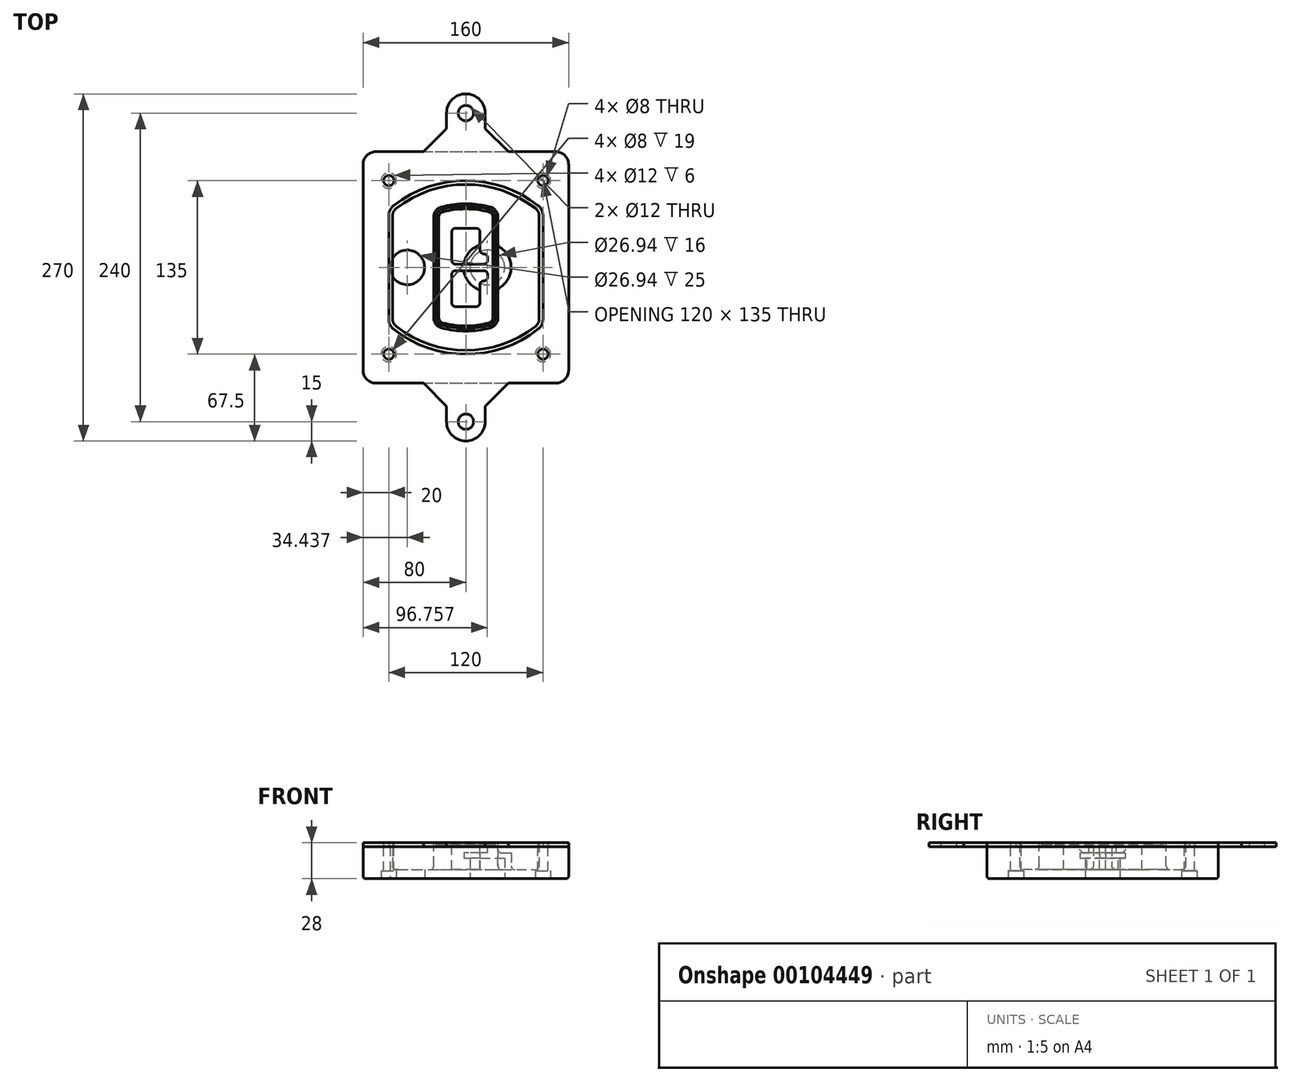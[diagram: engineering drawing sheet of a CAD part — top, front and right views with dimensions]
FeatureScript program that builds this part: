
annotation { "Feature Type Name" : "Feature", "Feature Type Description" : "" }
export const myFeature = defineFeature(function(context is Context, id is Id, definition is map)
    precondition{}
    {
        {
            var Q0;
            Q0=qCreatedBy(makeId("Top.planeOp"),FACE);
            var sketch = newSketch(context, id + "F0", { "sketchPlane" : qUnion([Q0])});
            skPoint(sketch, "E0.rect.middle", {"position": v(0, 0) * mm});
            skLineSegment(sketch, "E1.bottom", {"start": v(-70, -90) * mm, "end": v(70, -90) * mm});
            skLineSegment(sketch, "E1.top", {"start": v(-70, 90) * mm, "end": v(70, 90) * mm});
            skLineSegment(sketch, "E1.left", {"start": v(-80, -80) * mm, "end": v(-80, 80) * mm});
            skLineSegment(sketch, "E1.right", {"start": v(80, -80) * mm, "end": v(80, 80) * mm});
            skLineSegment(sketch, "E2", {"start": v(-80, 90) * mm, "end": v(80, -90) * mm, "construction": true});
            skLineSegment(sketch, "E3", {"start": v(80, 90) * mm, "end": v(-80, -90) * mm, "construction": true});
            skCircle(sketch, "E4", {"center": v(-60, 67.5) * mm, "radius": 4 * mm});
            skCircle(sketch, "E5", {"center": v(60, 67.5) * mm, "radius": 4 * mm});
            skCircle(sketch, "E6", {"center": v(60, -67.5) * mm, "radius": 4 * mm});
            skCircle(sketch, "E7", {"center": v(-60, -67.5) * mm, "radius": 4 * mm});
            skLineSegment(sketch, "E8", {"start": v(-60, 67.5) * mm, "end": v(60, 67.5) * mm, "construction": true});
            skLineSegment(sketch, "E9", {"start": v(60, 67.5) * mm, "end": v(60, -67.5) * mm, "construction": true});
            skLineSegment(sketch, "E10", {"start": v(60, -67.5) * mm, "end": v(-60, -67.5) * mm, "construction": true});
            skLineSegment(sketch, "E11", {"start": v(-60, -67.5) * mm, "end": v(-60, 67.5) * mm, "construction": true});
            skLineSegment(sketch, "E12", {"start": v(-60, 40.3) * mm, "end": v(-60, -40.3) * mm});
            skLineSegment(sketch, "E13", {"start": v(60, 40.3) * mm, "end": v(60, -40.3) * mm});
            skArc(sketch, "E14", {"start": v(56.15, 48.18) * mm, "mid": v(0, 67.5) * mm, "end": v(-56.15, 48.18) * mm});
            skArc(sketch, "E15", {"start": v(-56.15, -48.18) * mm, "mid": v(0, -67.5) * mm, "end": v(56.15, -48.18) * mm});
            skLineSegment(sketch, "E16", {"start": v(-60, 0) * mm, "end": v(60, 0) * mm, "construction": true});
            skPoint(sketch, "E17.visualSharp", {"position": v(-60, -45) * mm});
            skArc(sketch, "E17.filletArc", {"start": v(-60, -40.3) * mm, "mid": v(-58.99, -44.68) * mm, "end": v(-56.15, -48.18) * mm});
            skPoint(sketch, "E18.visualSharp", {"position": v(-60, 45) * mm});
            skArc(sketch, "E18.filletArc", {"start": v(-56.15, 48.18) * mm, "mid": v(-58.99, 44.68) * mm, "end": v(-60, 40.3) * mm});
            skPoint(sketch, "E19.visualSharp", {"position": v(60, 45) * mm});
            skArc(sketch, "E19.filletArc", {"start": v(60, 40.3) * mm, "mid": v(58.99, 44.68) * mm, "end": v(56.15, 48.18) * mm});
            skPoint(sketch, "E20.visualSharp", {"position": v(60, -45) * mm});
            skArc(sketch, "E20.filletArc", {"start": v(56.15, -48.18) * mm, "mid": v(58.99, -44.68) * mm, "end": v(60, -40.3) * mm});
            skPoint(sketch, "E21.visualSharp", {"position": v(-80, 90) * mm});
            skArc(sketch, "E21.filletArc", {"start": v(-70, 90) * mm, "mid": v(-77.07, 87.07) * mm, "end": v(-80, 80) * mm});
            skPoint(sketch, "E22.visualSharp", {"position": v(80, 90) * mm});
            skArc(sketch, "E22.filletArc", {"start": v(80, 80) * mm, "mid": v(77.07, 87.07) * mm, "end": v(70, 90) * mm});
            skPoint(sketch, "E23.visualSharp", {"position": v(80, -90) * mm});
            skArc(sketch, "E23.filletArc", {"start": v(70, -90) * mm, "mid": v(77.07, -87.07) * mm, "end": v(80, -80) * mm});
            skPoint(sketch, "E24.visualSharp", {"position": v(-80, -90) * mm});
            skArc(sketch, "E24.filletArc", {"start": v(-80, -80) * mm, "mid": v(-77.07, -87.07) * mm, "end": v(-70, -90) * mm});
            skArc(sketch, "E25.0", {"start": v(57, 40.3) * mm, "mid": v(56.3, 43.36) * mm, "end": v(54.3, 45.81) * mm});
            skLineSegment(sketch, "E25.1", {"start": v(57, 40.3) * mm, "end": v(57, -40.3) * mm});
            skArc(sketch, "E25.2", {"start": v(54.3, -45.81) * mm, "mid": v(56.3, -43.36) * mm, "end": v(57, -40.3) * mm});
            skArc(sketch, "E25.3", {"start": v(-54.3, -45.81) * mm, "mid": v(0, -64.5) * mm, "end": v(54.3, -45.81) * mm});
            skArc(sketch, "E25.4", {"start": v(-57, -40.3) * mm, "mid": v(-56.3, -43.36) * mm, "end": v(-54.3, -45.81) * mm});
            skArc(sketch, "E25.5", {"start": v(54.3, 45.81) * mm, "mid": v(0, 64.5) * mm, "end": v(-54.3, 45.81) * mm});
            skLineSegment(sketch, "E25.6", {"start": v(-57, 40.3) * mm, "end": v(-57, -40.3) * mm});
            skArc(sketch, "E25.7", {"start": v(-54.3, 45.81) * mm, "mid": v(-56.3, 43.36) * mm, "end": v(-57, 40.3) * mm});
            skArc(sketch, "E26.0", {"start": v(-58.62, 51.33) * mm, "mid": v(-62.58, 46.43) * mm, "end": v(-64, 40.3) * mm});
            skArc(sketch, "E26.1", {"start": v(58.62, 51.33) * mm, "mid": v(0, 71.5) * mm, "end": v(-58.62, 51.33) * mm});
            skArc(sketch, "E26.2", {"start": v(64, 40.3) * mm, "mid": v(62.58, 46.43) * mm, "end": v(58.62, 51.33) * mm});
            skLineSegment(sketch, "E26.3", {"start": v(64, 40.3) * mm, "end": v(64, -40.3) * mm});
            skArc(sketch, "E26.4", {"start": v(58.62, -51.33) * mm, "mid": v(62.58, -46.43) * mm, "end": v(64, -40.3) * mm});
            skLineSegment(sketch, "E26.5", {"start": v(-64, 40.3) * mm, "end": v(-64, -40.3) * mm});
            skArc(sketch, "E26.6", {"start": v(-58.62, -51.33) * mm, "mid": v(0, -71.5) * mm, "end": v(58.62, -51.33) * mm});
            skArc(sketch, "E26.7", {"start": v(-64, -40.3) * mm, "mid": v(-62.58, -46.43) * mm, "end": v(-58.62, -51.33) * mm});
            skSolve(sketch);
        }
        {
            var Q0;
            Q0=makeQuery(id+"F0.imprint","IMPRINT",FACE,{"disambiguationData":[TD([[makeQuery(id+"F0.imprint","IMPRINT",EDGE,{"derivedFrom":sQuery(id+"F0.wireOp",EDGE,"E1.bottom")}),1.0]])]});
            var Q1;
            Q1=makeQuery(id+"F0.imprint","IMPRINT",FACE,{"disambiguationData":[TD([[makeQuery(id+"F0.imprint","IMPRINT",EDGE,{"derivedFrom":sQuery(id+"F0.wireOp",EDGE,"E12")}),1.0]])]});
            var Q2;
            Q2=makeQuery(id+"F0.imprint","IMPRINT",FACE,{"disambiguationData":[TD([[makeQuery(id+"F0.imprint","IMPRINT",EDGE,{"derivedFrom":sQuery(id+"F0.wireOp",EDGE,"E25.0")}),1.0]])]});
            var Q3;
            Q3=makeQuery(id+"F0.imprint","IMPRINT",FACE,{"disambiguationData":[TD([[makeQuery(id+"F0.imprint","IMPRINT",EDGE,{"derivedFrom":sQuery(id+"F0.wireOp",EDGE,"E12")}),-1.0]])]});
            extrude(context, id + "F1", {"entities" : qUnion([Q0, Q1, Q2, Q3]), "oppositeDirection" : true, "depth" : 25 * mm});
        }
        {
            var Q0;
            Q0=makeQuery(id+"F0.imprint","IMPRINT",FACE,{"disambiguationData":[TD([[makeQuery(id+"F0.imprint","IMPRINT",EDGE,{"derivedFrom":sQuery(id+"F0.wireOp",EDGE,"E12")}),1.0]])]});
            extrude(context, id + "F2", {"entities" : qUnion([Q0]), "operationType" : NewBodyOperationType.ADD, "depth" : 3 * mm});
        }
        {
            var Q0;
            Q0=makeQuery(id+"F0.imprint","IMPRINT",FACE,{"disambiguationData":[TD([[makeQuery(id+"F0.imprint","IMPRINT",EDGE,{"derivedFrom":sQuery(id+"F0.wireOp",EDGE,"E25.0")}),1.0]])]});
            extrude(context, id + "F3", {"entities" : qUnion([Q0]), "operationType" : NewBodyOperationType.REMOVE, "oppositeDirection" : true, "depth" : 18 * mm});
        }
        {
            var Q0;
            Q0=makeQuery(id+"F2.opExtrude","CAP_FACE",FACE,{"disambiguationData":[OSD([sQuery(id+"F0.wireOp",EDGE,"E12"),sQuery(id+"F0.wireOp",EDGE,"E13"),sQuery(id+"F0.wireOp",EDGE,"E14"),sQuery(id+"F0.wireOp",EDGE,"E15"),sQuery(id+"F0.wireOp",EDGE,"E17.filletArc"),sQuery(id+"F0.wireOp",EDGE,"E18.filletArc"),sQuery(id+"F0.wireOp",EDGE,"E19.filletArc"),sQuery(id+"F0.wireOp",EDGE,"E20.filletArc"),sQuery(id+"F0.wireOp",EDGE,"E25.0"),sQuery(id+"F0.wireOp",EDGE,"E25.1"),sQuery(id+"F0.wireOp",EDGE,"E25.2"),sQuery(id+"F0.wireOp",EDGE,"E25.3"),sQuery(id+"F0.wireOp",EDGE,"E25.4"),sQuery(id+"F0.wireOp",EDGE,"E25.5"),sQuery(id+"F0.wireOp",EDGE,"E25.6"),sQuery(id+"F0.wireOp",EDGE,"E25.7")])],"isStart":false});
            var sketch = newSketch(context, id + "F4", { "sketchPlane" : qUnion([Q0])});
            skArc(sketch, "E27.0", {"start": v(-19.08, -46.97) * mm, "mid": v(0, -49.5) * mm, "end": v(19.08, -46.97) * mm});
            skArc(sketch, "E28.0", {"start": v(19.08, 46.97) * mm, "mid": v(0, 49.5) * mm, "end": v(-19.08, 46.97) * mm});
            skLineSegment(sketch, "E29", {"start": v(-25, 39.25) * mm, "end": v(-25, -39.25) * mm});
            skLineSegment(sketch, "E30", {"start": v(25, 39.25) * mm, "end": v(25, -39.25) * mm});
            skLineSegment(sketch, "E31", {"start": v(-25, 45.1) * mm, "end": v(25, 45.1) * mm, "construction": true});
            skLineSegment(sketch, "E32", {"start": v(-25, -45.1) * mm, "end": v(25, -45.1) * mm, "construction": true});
            skPoint(sketch, "E33.visualSharp", {"position": v(-25, 45.1) * mm});
            skArc(sketch, "E33.filletArc", {"start": v(-19.08, 46.97) * mm, "mid": v(-23.35, 44.11) * mm, "end": v(-25, 39.25) * mm});
            skPoint(sketch, "E34.visualSharp", {"position": v(25, 45.1) * mm});
            skArc(sketch, "E34.filletArc", {"start": v(25, 39.25) * mm, "mid": v(23.35, 44.11) * mm, "end": v(19.08, 46.97) * mm});
            skPoint(sketch, "E35.visualSharp", {"position": v(25, -45.1) * mm});
            skArc(sketch, "E35.filletArc", {"start": v(19.08, -46.97) * mm, "mid": v(23.35, -44.11) * mm, "end": v(25, -39.25) * mm});
            skPoint(sketch, "E36.visualSharp", {"position": v(-25, -45.1) * mm});
            skArc(sketch, "E36.filletArc", {"start": v(-25, -39.25) * mm, "mid": v(-23.35, -44.11) * mm, "end": v(-19.08, -46.97) * mm});
            skArc(sketch, "E37.0", {"start": v(54.3, 45.81) * mm, "mid": v(0, 64.5) * mm, "end": v(-54.3, 45.81) * mm});
            skArc(sketch, "E37.1", {"start": v(-54.3, 45.81) * mm, "mid": v(-56.3, 43.36) * mm, "end": v(-57, 40.3) * mm});
            skLineSegment(sketch, "E37.2", {"start": v(-57, 40.3) * mm, "end": v(-57, -40.3) * mm});
            skArc(sketch, "E37.3", {"start": v(-57, -40.3) * mm, "mid": v(-56.3, -43.36) * mm, "end": v(-54.3, -45.81) * mm});
            skArc(sketch, "E37.4", {"start": v(-54.3, -45.81) * mm, "mid": v(0, -64.5) * mm, "end": v(54.3, -45.81) * mm});
            skArc(sketch, "E37.5", {"start": v(54.3, -45.81) * mm, "mid": v(56.3, -43.36) * mm, "end": v(57, -40.3) * mm});
            skLineSegment(sketch, "E37.6", {"start": v(57, 40.3) * mm, "end": v(57, -40.3) * mm});
            skArc(sketch, "E37.7", {"start": v(57, 40.3) * mm, "mid": v(56.3, 43.36) * mm, "end": v(54.3, 45.81) * mm});
            skLineSegment(sketch, "E38.0", {"start": v(23, 39.25) * mm, "end": v(23, -39.25) * mm});
            skArc(sketch, "E38.1", {"start": v(18.56, -45.04) * mm, "mid": v(21.76, -42.9) * mm, "end": v(23, -39.25) * mm});
            skArc(sketch, "E38.2", {"start": v(-18.56, -45.04) * mm, "mid": v(0, -47.5) * mm, "end": v(18.56, -45.04) * mm});
            skArc(sketch, "E38.3", {"start": v(-23, -39.25) * mm, "mid": v(-21.76, -42.9) * mm, "end": v(-18.56, -45.04) * mm});
            skLineSegment(sketch, "E38.4", {"start": v(-23, 39.25) * mm, "end": v(-23, -39.25) * mm});
            skArc(sketch, "E38.5", {"start": v(23, 39.25) * mm, "mid": v(21.76, 42.9) * mm, "end": v(18.56, 45.04) * mm});
            skArc(sketch, "E38.6", {"start": v(-18.56, 45.04) * mm, "mid": v(-21.76, 42.9) * mm, "end": v(-23, 39.25) * mm});
            skArc(sketch, "E38.7", {"start": v(18.56, 45.04) * mm, "mid": v(0, 47.5) * mm, "end": v(-18.56, 45.04) * mm});
            skArc(sketch, "E39.0", {"start": v(21, 39.25) * mm, "mid": v(20.18, 41.68) * mm, "end": v(18.04, 43.1) * mm});
            skLineSegment(sketch, "E39.1", {"start": v(21, 39.25) * mm, "end": v(21, -39.25) * mm});
            skArc(sketch, "E39.2", {"start": v(18.04, -43.1) * mm, "mid": v(20.18, -41.68) * mm, "end": v(21, -39.25) * mm});
            skArc(sketch, "E39.3", {"start": v(-18.04, -43.1) * mm, "mid": v(0, -45.5) * mm, "end": v(18.04, -43.1) * mm});
            skArc(sketch, "E39.4", {"start": v(-21, -39.25) * mm, "mid": v(-20.18, -41.68) * mm, "end": v(-18.04, -43.1) * mm});
            skArc(sketch, "E39.5", {"start": v(18.04, 43.1) * mm, "mid": v(0, 45.5) * mm, "end": v(-18.04, 43.1) * mm});
            skLineSegment(sketch, "E39.6", {"start": v(-21, 39.25) * mm, "end": v(-21, -39.25) * mm});
            skArc(sketch, "E39.7", {"start": v(-18.04, 43.1) * mm, "mid": v(-20.18, 41.68) * mm, "end": v(-21, 39.25) * mm});
            skLineSegment(sketch, "E40", {"start": v(-25, 0) * mm, "end": v(25, 0) * mm, "construction": true});
            skLineSegment(sketch, "E41", {"start": v(-11, 5.5) * mm, "end": v(-11, 27.5) * mm});
            skLineSegment(sketch, "E42", {"start": v(-8, 30.5) * mm, "end": v(8, 30.5) * mm});
            skLineSegment(sketch, "E43", {"start": v(11, 27.5) * mm, "end": v(11, 13.5) * mm});
            skLineSegment(sketch, "E44", {"start": v(14, 10.5) * mm, "end": v(14, 10.5) * mm});
            skLineSegment(sketch, "E45", {"start": v(17, 7.5) * mm, "end": v(17, 5.5) * mm});
            skLineSegment(sketch, "E46", {"start": v(14, 2.5) * mm, "end": v(-8, 2.5) * mm});
            skPoint(sketch, "E47.visualSharp", {"position": v(-11, 30.5) * mm});
            skArc(sketch, "E47.filletArc", {"start": v(-8, 30.5) * mm, "mid": v(-10.12, 29.62) * mm, "end": v(-11, 27.5) * mm});
            skPoint(sketch, "E48.visualSharp", {"position": v(11, 30.5) * mm});
            skArc(sketch, "E48.filletArc", {"start": v(11, 27.5) * mm, "mid": v(10.12, 29.62) * mm, "end": v(8, 30.5) * mm});
            skPoint(sketch, "E49.visualSharp", {"position": v(11, 10.5) * mm});
            skArc(sketch, "E49.filletArc", {"start": v(11, 13.5) * mm, "mid": v(11.88, 11.38) * mm, "end": v(14, 10.5) * mm});
            skPoint(sketch, "E50.visualSharp", {"position": v(17, 10.5) * mm});
            skArc(sketch, "E50.filletArc", {"start": v(17, 7.5) * mm, "mid": v(16.12, 9.62) * mm, "end": v(14, 10.5) * mm});
            skPoint(sketch, "E51.visualSharp", {"position": v(17, 2.5) * mm});
            skArc(sketch, "E51.filletArc", {"start": v(14, 2.5) * mm, "mid": v(16.12, 3.38) * mm, "end": v(17, 5.5) * mm});
            skPoint(sketch, "E52.visualSharp", {"position": v(-11, 2.5) * mm});
            skArc(sketch, "E52.filletArc", {"start": v(-11, 5.5) * mm, "mid": v(-10.12, 3.38) * mm, "end": v(-8, 2.5) * mm});
            skLineSegment(sketch, "E53.0.MirrorCS", {"start": v(14, -2.5) * mm, "end": v(-8, -2.5) * mm});
            skArc(sketch, "E54.0.MirrorCS", {"start": v(-11, -5.5) * mm, "mid": v(-10.12, -3.38) * mm, "end": v(-8, -2.5) * mm});
            skLineSegment(sketch, "E55.0.MirrorCS", {"start": v(-11, -5.5) * mm, "end": v(-11, -27.5) * mm});
            skArc(sketch, "E56.0.MirrorCS", {"start": v(-8, -30.5) * mm, "mid": v(-10.12, -29.62) * mm, "end": v(-11, -27.5) * mm});
            skLineSegment(sketch, "E57.0.MirrorCS", {"start": v(-8, -30.5) * mm, "end": v(8, -30.5) * mm});
            skArc(sketch, "E58.0.MirrorCS", {"start": v(11, -27.5) * mm, "mid": v(10.12, -29.62) * mm, "end": v(8, -30.5) * mm});
            skLineSegment(sketch, "E59.0.MirrorCS", {"start": v(11, -27.5) * mm, "end": v(11, -13.5) * mm});
            skArc(sketch, "E60.0.MirrorCS", {"start": v(11, -13.5) * mm, "mid": v(11.88, -11.38) * mm, "end": v(14, -10.5) * mm});
            skArc(sketch, "E61.0.MirrorCS", {"start": v(17, -7.5) * mm, "mid": v(16.12, -9.62) * mm, "end": v(14, -10.5) * mm});
            skLineSegment(sketch, "E62.0.MirrorCS", {"start": v(17, -7.5) * mm, "end": v(17, -5.5) * mm});
            skArc(sketch, "E63.0.MirrorCS", {"start": v(14, -2.5) * mm, "mid": v(16.12, -3.38) * mm, "end": v(17, -5.5) * mm});
            skSolve(sketch);
        }
        {
            var Q0;
            Q0=makeQuery(id+"F4.imprint","IMPRINT",FACE,{"disambiguationData":[TD([[makeQuery(id+"F4.imprint","IMPRINT",EDGE,{"derivedFrom":sQuery(id+"F4.wireOp",EDGE,"E27.0")}),1.0]])]});
            var Q1;
            Q1=makeQuery(id+"F4.imprint","IMPRINT",FACE,{"disambiguationData":[TD([[makeQuery(id+"F4.imprint","IMPRINT",EDGE,{"derivedFrom":sQuery(id+"F4.wireOp",EDGE,"E38.0")}),-1.0]])]});
            var Q2;
            Q2=makeQuery(id+"F4.imprint","IMPRINT",FACE,{"disambiguationData":[TD([[makeQuery(id+"F4.imprint","IMPRINT",EDGE,{"derivedFrom":sQuery(id+"F4.wireOp",EDGE,"E39.0")}),1.0]])]});
            extrude(context, id + "F5", {"entities" : qUnion([Q0, Q1, Q2]), "operationType" : NewBodyOperationType.ADD, "endBound" : BoundingType.UP_TO_NEXT, "oppositeDirection" : true, "depth" : 25 * mm});
        }
        {
            var Q0;
            Q0=makeQuery(id+"F4.imprint","IMPRINT",FACE,{"disambiguationData":[TD([[makeQuery(id+"F4.imprint","IMPRINT",EDGE,{"derivedFrom":sQuery(id+"F4.wireOp",EDGE,"E38.0")}),-1.0]])]});
            extrude(context, id + "F6", {"entities" : qUnion([Q0]), "operationType" : NewBodyOperationType.REMOVE, "oppositeDirection" : true, "depth" : 2 * mm});
        }
        {
            var Q0;
            Q0=makeQuery(id+"F1.opExtrude","CAP_FACE",FACE,{"disambiguationData":[OSD([sQuery(id+"F0.wireOp",EDGE,"E1.bottom"),sQuery(id+"F0.wireOp",EDGE,"E1.top"),sQuery(id+"F0.wireOp",EDGE,"E1.left"),sQuery(id+"F0.wireOp",EDGE,"E1.right"),sQuery(id+"F0.wireOp",EDGE,"E4"),sQuery(id+"F0.wireOp",EDGE,"E5"),sQuery(id+"F0.wireOp",EDGE,"E6"),sQuery(id+"F0.wireOp",EDGE,"E7"),sQuery(id+"F0.wireOp",EDGE,"E21.filletArc"),sQuery(id+"F0.wireOp",EDGE,"E22.filletArc"),sQuery(id+"F0.wireOp",EDGE,"E23.filletArc"),sQuery(id+"F0.wireOp",EDGE,"E24.filletArc")])],"isStart":false});
            var sketch = newSketch(context, id + "F7", { "sketchPlane" : qUnion([Q0])});
            skCircle(sketch, "E64", {"center": v(16.76, 0) * mm, "radius": 13.47 * mm});
            skCircle(sketch, "E65", {"center": v(-45.56, 0) * mm, "radius": 13.47 * mm});
            skLineSegment(sketch, "E66", {"start": v(80, 0) * mm, "end": v(-80, 0) * mm});
            skCircle(sketch, "E67", {"center": v(16.76, 0) * mm, "radius": 18.47 * mm});
            skCircle(sketch, "E68", {"center": v(60, -67.5) * mm, "radius": 6 * mm});
            skCircle(sketch, "E69", {"center": v(-60, -67.5) * mm, "radius": 6 * mm});
            skCircle(sketch, "E70", {"center": v(-60, 67.5) * mm, "radius": 6 * mm});
            skCircle(sketch, "E71", {"center": v(60, 67.5) * mm, "radius": 6 * mm});
            skSolve(sketch);
        }
        {
            var Q0;
            {var subQ1=sQuery(id+"F7.wireOp",EDGE,"E66");var subQ4=sQuery(id+"F7.wireOp",EDGE,"E64");var subQ6=makeQuery(id+"F7.imprint","INTERSECT",VERTEX,{"disambiguationData":[OD(0.0)],"derivedFrom":[subQ4,subQ1]});Q0=makeQuery(id+"F7.imprint","IMPRINT",FACE,{"disambiguationData":[TD([[makeQuery(id+"F7.imprint","IMPRINT",EDGE,{"disambiguationData":[TD([[subQ6,-1.0]])],"derivedFrom":subQ4}),-1.0]])]});}
            var Q1;
            {var subQ0=sQuery(id+"F7.wireOp",EDGE,"E66");var subQ1=sQuery(id+"F7.wireOp",EDGE,"E64");var subQ3=makeQuery(id+"F7.imprint","INTERSECT",VERTEX,{"disambiguationData":[OD(0.0)],"derivedFrom":[subQ1,subQ0]});Q1=makeQuery(id+"F7.imprint","IMPRINT",FACE,{"disambiguationData":[TD([[makeQuery(id+"F7.imprint","IMPRINT",EDGE,{"disambiguationData":[TD([[subQ3,-1.0]])],"derivedFrom":subQ1}),1.0]])]});}
            var Q2;
            {var subQ0=sQuery(id+"F7.wireOp",EDGE,"E66");var subQ1=sQuery(id+"F7.wireOp",EDGE,"E64");var subQ3=makeQuery(id+"F7.imprint","INTERSECT",VERTEX,{"disambiguationData":[OD(0.0)],"derivedFrom":[subQ1,subQ0]});Q2=makeQuery(id+"F7.imprint","IMPRINT",FACE,{"disambiguationData":[TD([[makeQuery(id+"F7.imprint","IMPRINT",EDGE,{"disambiguationData":[TD([[subQ3,1.0]])],"derivedFrom":subQ1}),1.0]])]});}
            var Q3;
            {var subQ1=sQuery(id+"F7.wireOp",EDGE,"E66");var subQ4=sQuery(id+"F7.wireOp",EDGE,"E64");var subQ6=makeQuery(id+"F7.imprint","INTERSECT",VERTEX,{"disambiguationData":[OD(0.0)],"derivedFrom":[subQ4,subQ1]});Q3=makeQuery(id+"F7.imprint","IMPRINT",FACE,{"disambiguationData":[TD([[makeQuery(id+"F7.imprint","IMPRINT",EDGE,{"disambiguationData":[TD([[subQ6,1.0]])],"derivedFrom":subQ4}),-1.0]])]});}
            extrude(context, id + "F8", {"entities" : qUnion([Q0, Q1, Q2, Q3]), "operationType" : NewBodyOperationType.ADD, "oppositeDirection" : true, "depth" : 20 * mm});
        }
        {
            var Q0;
            {var subQ0=sQuery(id+"F7.wireOp",EDGE,"E66");var subQ1=sQuery(id+"F7.wireOp",EDGE,"E64");var subQ3=makeQuery(id+"F7.imprint","INTERSECT",VERTEX,{"disambiguationData":[OD(0.0)],"derivedFrom":[subQ1,subQ0]});Q0=makeQuery(id+"F7.imprint","IMPRINT",FACE,{"disambiguationData":[TD([[makeQuery(id+"F7.imprint","IMPRINT",EDGE,{"disambiguationData":[TD([[subQ3,-1.0]])],"derivedFrom":subQ1}),1.0]])]});}
            var Q1;
            {var subQ0=sQuery(id+"F7.wireOp",EDGE,"E66");var subQ1=sQuery(id+"F7.wireOp",EDGE,"E64");var subQ3=makeQuery(id+"F7.imprint","INTERSECT",VERTEX,{"disambiguationData":[OD(0.0)],"derivedFrom":[subQ1,subQ0]});Q1=makeQuery(id+"F7.imprint","IMPRINT",FACE,{"disambiguationData":[TD([[makeQuery(id+"F7.imprint","IMPRINT",EDGE,{"disambiguationData":[TD([[subQ3,1.0]])],"derivedFrom":subQ1}),1.0]])]});}
            extrude(context, id + "F9", {"entities" : qUnion([Q0, Q1]), "operationType" : NewBodyOperationType.REMOVE, "oppositeDirection" : true, "depth" : 16 * mm});
        }
        {
            var Q0;
            {var subQ0=sQuery(id+"F7.wireOp",EDGE,"E66");var subQ1=sQuery(id+"F7.wireOp",EDGE,"E65");var subQ3=makeQuery(id+"F7.imprint","INTERSECT",VERTEX,{"disambiguationData":[OD(0.0)],"derivedFrom":[subQ1,subQ0]});Q0=makeQuery(id+"F7.imprint","IMPRINT",FACE,{"disambiguationData":[TD([[makeQuery(id+"F7.imprint","IMPRINT",EDGE,{"disambiguationData":[TD([[subQ3,-1.0]])],"derivedFrom":subQ1}),1.0]])]});}
            var Q1;
            {var subQ0=sQuery(id+"F7.wireOp",EDGE,"E66");var subQ1=sQuery(id+"F7.wireOp",EDGE,"E65");var subQ3=makeQuery(id+"F7.imprint","INTERSECT",VERTEX,{"disambiguationData":[OD(0.0)],"derivedFrom":[subQ1,subQ0]});Q1=makeQuery(id+"F7.imprint","IMPRINT",FACE,{"disambiguationData":[TD([[makeQuery(id+"F7.imprint","IMPRINT",EDGE,{"disambiguationData":[TD([[subQ3,1.0]])],"derivedFrom":subQ1}),1.0]])]});}
            extrude(context, id + "F10", {"entities" : qUnion([Q0, Q1]), "operationType" : NewBodyOperationType.REMOVE, "oppositeDirection" : true, "depth" : 25 * mm});
        }
        {
            var Q0;
            Q0=makeQuery(id+"F7.imprint","IMPRINT",FACE,{"disambiguationData":[TD([[makeQuery(id+"F7.imprint","IMPRINT",EDGE,{"derivedFrom":sQuery(id+"F7.wireOp",EDGE,"E68")}),1.0]])]});
            var Q1;
            Q1=makeQuery(id+"F7.imprint","IMPRINT",FACE,{"disambiguationData":[TD([[makeQuery(id+"F7.imprint","IMPRINT",EDGE,{"derivedFrom":makeQuery(id+"F1.opExtrude","CAP_EDGE",EDGE,{"disambiguationData":[OSD([sQuery(id+"F0.wireOp",EDGE,"E5")])],"isStart":false})}),-1.0]])]});
            var Q2;
            Q2=makeQuery(id+"F7.imprint","IMPRINT",FACE,{"disambiguationData":[TD([[makeQuery(id+"F7.imprint","IMPRINT",EDGE,{"derivedFrom":sQuery(id+"F7.wireOp",EDGE,"E69")}),1.0]])]});
            var Q3;
            Q3=makeQuery(id+"F7.imprint","IMPRINT",FACE,{"disambiguationData":[TD([[makeQuery(id+"F7.imprint","IMPRINT",EDGE,{"derivedFrom":makeQuery(id+"F1.opExtrude","CAP_EDGE",EDGE,{"disambiguationData":[OSD([sQuery(id+"F0.wireOp",EDGE,"E4")])],"isStart":false})}),-1.0]])]});
            var Q4;
            Q4=makeQuery(id+"F7.imprint","IMPRINT",FACE,{"disambiguationData":[TD([[makeQuery(id+"F7.imprint","IMPRINT",EDGE,{"derivedFrom":sQuery(id+"F7.wireOp",EDGE,"E70")}),1.0]])]});
            var Q5;
            Q5=makeQuery(id+"F7.imprint","IMPRINT",FACE,{"disambiguationData":[TD([[makeQuery(id+"F7.imprint","IMPRINT",EDGE,{"derivedFrom":makeQuery(id+"F1.opExtrude","CAP_EDGE",EDGE,{"disambiguationData":[OSD([sQuery(id+"F0.wireOp",EDGE,"E7")])],"isStart":false})}),-1.0]])]});
            var Q6;
            Q6=makeQuery(id+"F7.imprint","IMPRINT",FACE,{"disambiguationData":[TD([[makeQuery(id+"F7.imprint","IMPRINT",EDGE,{"derivedFrom":sQuery(id+"F7.wireOp",EDGE,"E71")}),1.0]])]});
            var Q7;
            Q7=makeQuery(id+"F7.imprint","IMPRINT",FACE,{"disambiguationData":[TD([[makeQuery(id+"F7.imprint","IMPRINT",EDGE,{"derivedFrom":makeQuery(id+"F1.opExtrude","CAP_EDGE",EDGE,{"disambiguationData":[OSD([sQuery(id+"F0.wireOp",EDGE,"E6")])],"isStart":false})}),-1.0]])]});
            extrude(context, id + "F11", {"entities" : qUnion([Q0, Q1, Q2, Q3, Q4, Q5, Q6, Q7]), "operationType" : NewBodyOperationType.REMOVE, "oppositeDirection" : true, "depth" : 6 * mm});
        }
        {
            var Q0;
            Q0=makeQuery(id+"F9.boolean.opBoolean","COPY",FACE,{"derivedFrom":makeQuery(id+"F9.opExtrude","CAP_FACE",FACE,{"disambiguationData":[OSD([sQuery(id+"F7.wireOp",EDGE,"E64")])],"isStart":false})});
            var sketch = newSketch(context, id + "F12", { "sketchPlane" : qUnion([Q0])});
            skArc(sketch, "E72.0", {"start": v(11, 17.55) * mm, "mid": v(2.57, 11.82) * mm, "end": v(-1.54, 2.5) * mm});
            skArc(sketch, "E72.1", {"start": v(-1.54, -2.5) * mm, "mid": v(2.57, -11.82) * mm, "end": v(11, -17.55) * mm});
            skLineSegment(sketch, "E73", {"start": v(-1.54, -2.5) * mm, "end": v(14, -2.5) * mm});
            skLineSegment(sketch, "E74.0", {"start": v(14, 2.5) * mm, "end": v(-1.54, 2.5) * mm});
            skArc(sketch, "E74.1", {"start": v(14, 2.5) * mm, "mid": v(16.12, 3.38) * mm, "end": v(17, 5.5) * mm});
            skLineSegment(sketch, "E74.2", {"start": v(17, 7.5) * mm, "end": v(17, 5.5) * mm});
            skArc(sketch, "E74.3", {"start": v(17, 7.5) * mm, "mid": v(16.12, 9.62) * mm, "end": v(14, 10.5) * mm});
            skArc(sketch, "E74.4", {"start": v(11, 13.5) * mm, "mid": v(11.88, 11.38) * mm, "end": v(14, 10.5) * mm});
            skLineSegment(sketch, "E74.5", {"start": v(11, 17.55) * mm, "end": v(11, 13.5) * mm});
            skLineSegment(sketch, "E74.7", {"start": v(14, -2.5) * mm, "end": v(-1.54, -2.5) * mm});
            skArc(sketch, "E74.8", {"start": v(14, -2.5) * mm, "mid": v(16.12, -3.38) * mm, "end": v(17, -5.5) * mm});
            skLineSegment(sketch, "E74.9", {"start": v(17, -7.5) * mm, "end": v(17, -5.5) * mm});
            skArc(sketch, "E74.10", {"start": v(17, -7.5) * mm, "mid": v(16.12, -9.62) * mm, "end": v(14, -10.5) * mm});
            skArc(sketch, "E74.11", {"start": v(11, -13.5) * mm, "mid": v(11.88, -11.38) * mm, "end": v(14, -10.5) * mm});
            skLineSegment(sketch, "E74.12", {"start": v(11, -17.55) * mm, "end": v(11, -13.5) * mm});
            skPoint(sketch, "E75.orphan", {"position": v(11, -27.5) * mm});
            skPoint(sketch, "E76.orphan", {"position": v(-8, -2.5) * mm});
            skPoint(sketch, "E77.orphan", {"position": v(-8, 2.5) * mm});
            skPoint(sketch, "E78.orphan", {"position": v(11, 27.5) * mm});
            skSolve(sketch);
        }
        {
            var Q0;
            {var subQ7=sQuery(id+"F12.wireOp",EDGE,"E72.0");var subQ14=sQuery(id+"F12.wireOp",EDGE,"E72.1");var subQ16=sQuery(id+"F12.wireOp",EDGE,"E74.1");var subQ18=sQuery(id+"F12.wireOp",EDGE,"E74.8");Q0=qUnion([makeQuery(id+"F12.imprint","IMPRINT",FACE,{"disambiguationData":[TD([[makeQuery(id+"F12.imprint","IMPRINT",EDGE,{"derivedFrom":subQ7}),1.0]])]}),makeQuery(id+"F12.imprint","IMPRINT",FACE,{"disambiguationData":[TD([[makeQuery(id+"F12.imprint","IMPRINT",EDGE,{"derivedFrom":subQ14}),1.0]])]}),makeQuery(id+"F12.imprint","IMPRINT",FACE,{"disambiguationData":[TD([[makeQuery(id+"F12.imprint","IMPRINT",EDGE,{"derivedFrom":subQ16}),1.0]])]}),makeQuery(id+"F12.imprint","IMPRINT",FACE,{"disambiguationData":[TD([[makeQuery(id+"F12.imprint","IMPRINT",EDGE,{"derivedFrom":subQ18}),-1.0]])]})]);}
            var Q1;
            Q1=makeQuery(id+"F5.boolean.opBoolean","SPLIT",FACE,{"disambiguationData":[TD([makeQuery(id+"F5.opExtrude","SWEPT_FACE",FACE,{"disambiguationData":[OSD([sQuery(id+"F4.wireOp",EDGE,"E41")])]})])],"derivedFrom":makeQuery(id+"F3.boolean.opBoolean","COPY",FACE,{"derivedFrom":makeQuery(id+"F3.opExtrude","CAP_FACE",FACE,{"disambiguationData":[OSD([sQuery(id+"F0.wireOp",EDGE,"E25.0"),sQuery(id+"F0.wireOp",EDGE,"E25.1"),sQuery(id+"F0.wireOp",EDGE,"E25.2"),sQuery(id+"F0.wireOp",EDGE,"E25.3"),sQuery(id+"F0.wireOp",EDGE,"E25.4"),sQuery(id+"F0.wireOp",EDGE,"E25.5"),sQuery(id+"F0.wireOp",EDGE,"E25.6"),sQuery(id+"F0.wireOp",EDGE,"E25.7")])],"isStart":false})})});
            extrude(context, id + "F13", {"entities" : qUnion([Q0]), "operationType" : NewBodyOperationType.REMOVE, "endBound" : BoundingType.UP_TO_SURFACE, "endBoundEntityFace" : qUnion([Q1]), "depth" : 25 * mm});
        }
        {
            var Q0;
            Q0=makeQuery(id+"F3.boolean.opBoolean","COPY",EDGE,{"derivedFrom":makeQuery(id+"F3.opExtrude","CAP_EDGE",EDGE,{"disambiguationData":[OSD([sQuery(id+"F0.wireOp",EDGE,"E25.6")])],"isStart":false})});
            var Q1;
            Q1=makeQuery(id+"F8.boolean.opBoolean","INTERSECT",EDGE,{"derivedFrom":[makeQuery(id+"F5.opExtrude","SWEPT_FACE",FACE,{"disambiguationData":[OSD([sQuery(id+"F4.wireOp",EDGE,"E30")])]}),makeQuery(id+"F8.opExtrude","CAP_FACE",FACE,{"disambiguationData":[OSD([sQuery(id+"F7.wireOp",EDGE,"E67")])],"isStart":false})]});
            var Q2;
            Q2=makeQuery(id+"F8.boolean.opBoolean","INTERSECT",EDGE,{"disambiguationData":[OD(1.0)],"derivedFrom":[makeQuery(id+"F5.opExtrude","SWEPT_FACE",FACE,{"disambiguationData":[OSD([sQuery(id+"F4.wireOp",EDGE,"E30")])]}),makeQuery(id+"F8.opExtrude","SWEPT_FACE",FACE,{"disambiguationData":[OSD([sQuery(id+"F7.wireOp",EDGE,"E67")])]})]});
            var Q3;
            {var subQ0=sQuery(id+"F4.wireOp",EDGE,"E30");Q3=makeQuery(id+"F8.boolean.opBoolean","SPLIT",EDGE,{"disambiguationData":[TD([makeQuery(id+"F5.opExtrude","SWEPT_FACE",FACE,{"disambiguationData":[OSD([sQuery(id+"F4.wireOp",EDGE,"E35.filletArc")])]})])],"derivedFrom":makeQuery(id+"F5.opExtrude","CAP_EDGE",EDGE,{"disambiguationData":[OSD([subQ0])],"isStart":false})});}
            var Q4;
            {var subQ0=sQuery(id+"F0.wireOp",EDGE,"E25.7");var subQ1=sQuery(id+"F0.wireOp",EDGE,"E25.1");var subQ2=sQuery(id+"F0.wireOp",EDGE,"E25.6");var subQ3=sQuery(id+"F0.wireOp",EDGE,"E25.5");var subQ4=sQuery(id+"F0.wireOp",EDGE,"E25.4");var subQ5=sQuery(id+"F0.wireOp",EDGE,"E25.0");var subQ6=sQuery(id+"F0.wireOp",EDGE,"E25.2");var subQ7=sQuery(id+"F0.wireOp",EDGE,"E25.3");Q4=makeQuery(id+"F8.boolean.opBoolean","INTERSECT",EDGE,{"derivedFrom":[makeQuery(id+"F5.boolean.opBoolean","SPLIT",FACE,{"disambiguationData":[TD([makeQuery(id+"F2.opExtrude","SWEPT_FACE",FACE,{"disambiguationData":[OSD([subQ5])]})])],"derivedFrom":makeQuery(id+"F3.boolean.opBoolean","COPY",FACE,{"derivedFrom":makeQuery(id+"F3.opExtrude","CAP_FACE",FACE,{"disambiguationData":[OSD([subQ5,subQ1,subQ6,subQ7,subQ4,subQ3,subQ2,subQ0])],"isStart":false})})}),makeQuery(id+"F8.opExtrude","SWEPT_FACE",FACE,{"disambiguationData":[OSD([sQuery(id+"F7.wireOp",EDGE,"E67")])]})]});}
            var Q5;
            Q5=makeQuery(id+"F8.boolean.opBoolean","INTERSECT",EDGE,{"disambiguationData":[OD(0.0)],"derivedFrom":[makeQuery(id+"F5.opExtrude","SWEPT_FACE",FACE,{"disambiguationData":[OSD([sQuery(id+"F4.wireOp",EDGE,"E30")])]}),makeQuery(id+"F8.opExtrude","SWEPT_FACE",FACE,{"disambiguationData":[OSD([sQuery(id+"F7.wireOp",EDGE,"E67")])]})]});
            fillet(context, id + "F14", {"entities" : qUnion([Q0, Q1, Q2, Q3, Q4, Q5]), "radius" : 3 * mm, "tangentPropagation" : true, "allowEdgeOverflow" : false});
        }
        {
            var Q0;
            Q0=makeQuery(id+"F1.opExtrude","CAP_EDGE",EDGE,{"disambiguationData":[OSD([sQuery(id+"F0.wireOp",EDGE,"E1.bottom")])],"isStart":false});
            fillet(context, id + "F15", {"entities" : qUnion([Q0]), "radius" : 2 * mm, "tangentPropagation" : true, "allowEdgeOverflow" : false});
        }
        {
            var Q0;
            {var subQ0=sQuery(id+"F0.wireOp",EDGE,"E22.filletArc");var subQ1=sQuery(id+"F0.wireOp",EDGE,"E7");var subQ2=sQuery(id+"F0.wireOp",EDGE,"E6");var subQ3=sQuery(id+"F0.wireOp",EDGE,"E5");var subQ4=sQuery(id+"F0.wireOp",EDGE,"E4");var subQ5=sQuery(id+"F0.wireOp",EDGE,"E1.bottom");var subQ6=sQuery(id+"F0.wireOp",EDGE,"E21.filletArc");var subQ7=sQuery(id+"F0.wireOp",EDGE,"E1.top");var subQ8=sQuery(id+"F0.wireOp",EDGE,"E1.left");var subQ9=sQuery(id+"F0.wireOp",EDGE,"E1.right");var subQ10=sQuery(id+"F0.wireOp",EDGE,"E23.filletArc");var subQ11=sQuery(id+"F0.wireOp",EDGE,"E24.filletArc");Q0=makeQuery(id+"F2.boolean.opBoolean","SPLIT",FACE,{"disambiguationData":[TD([makeQuery(id+"F1.opExtrude","SWEPT_FACE",FACE,{"disambiguationData":[OSD([subQ5])]})])],"derivedFrom":makeQuery(id+"F1.opExtrude","CAP_FACE",FACE,{"disambiguationData":[OSD([subQ5,subQ7,subQ8,subQ9,subQ4,subQ3,subQ2,subQ1,subQ6,subQ0,subQ10,subQ11])],"isStart":true})});}
            var sketch = newSketch(context, id + "F16", { "sketchPlane" : qUnion([Q0])});
            skCircle(sketch, "E79", {"center": v(0, 120) * mm, "radius": 6 * mm});
            skArc(sketch, "E80", {"start": v(-15, 120) * mm, "mid": v(0, 135) * mm, "end": v(15, 120) * mm});
            skLineSegment(sketch, "E81", {"start": v(-33, 90) * mm, "end": v(-15, 108) * mm});
            skLineSegment(sketch, "E82", {"start": v(-15, 108) * mm, "end": v(-15, 120) * mm});
            skLineSegment(sketch, "E83", {"start": v(15, 120) * mm, "end": v(15, 108) * mm});
            skLineSegment(sketch, "E84", {"start": v(15, 108) * mm, "end": v(33, 90) * mm});
            skLineSegment(sketch, "E85", {"start": v(-80, 0) * mm, "end": v(80, 0) * mm, "construction": true});
            skArc(sketch, "E86.MirrorCS", {"start": v(-15, -120) * mm, "mid": v(0, -135) * mm, "end": v(15, -120) * mm});
            skLineSegment(sketch, "E87.MirrorCS", {"start": v(15, -120) * mm, "end": v(15, -108) * mm});
            skCircle(sketch, "E88.MirrorC", {"center": v(0, -120) * mm, "radius": 6 * mm});
            skLineSegment(sketch, "E89.MirrorCS", {"start": v(-15, -108) * mm, "end": v(-15, -120) * mm});
            skLineSegment(sketch, "E90.MirrorCS", {"start": v(15, -108) * mm, "end": v(33, -90) * mm});
            skLineSegment(sketch, "E91.MirrorCS", {"start": v(-33, -90) * mm, "end": v(-15, -108) * mm});
            skLineSegment(sketch, "E92", {"start": v(0, 120) * mm, "end": v(0, 90) * mm, "construction": true});
            skCircle(sketch, "E93.8", {"center": v(-60, -67.5) * mm, "radius": 4 * mm});
            skCircle(sketch, "E93.9", {"center": v(-60, 67.5) * mm, "radius": 4 * mm});
            skCircle(sketch, "E93.10", {"center": v(60, 67.5) * mm, "radius": 4 * mm});
            skCircle(sketch, "E93.11", {"center": v(60, -67.5) * mm, "radius": 4 * mm});
            skArc(sketch, "E94.0", {"start": v(-70, 90) * mm, "mid": v(-77.07, 87.07) * mm, "end": v(-80, 80) * mm});
            skLineSegment(sketch, "E94.1", {"start": v(-80, -80) * mm, "end": v(-80, 80) * mm});
            skArc(sketch, "E94.2", {"start": v(-80, -80) * mm, "mid": v(-77.07, -87.07) * mm, "end": v(-70, -90) * mm});
            skLineSegment(sketch, "E94.3", {"start": v(-70, -90) * mm, "end": v(70, -90) * mm});
            skArc(sketch, "E94.4", {"start": v(70, -90) * mm, "mid": v(77.07, -87.07) * mm, "end": v(80, -80) * mm});
            skLineSegment(sketch, "E94.5", {"start": v(80, -80) * mm, "end": v(80, 80) * mm});
            skArc(sketch, "E94.6", {"start": v(80, 80) * mm, "mid": v(77.07, 87.07) * mm, "end": v(70, 90) * mm});
            skLineSegment(sketch, "E94.7", {"start": v(-70, 90) * mm, "end": v(70, 90) * mm});
            skArc(sketch, "E94.8", {"start": v(56.15, 48.18) * mm, "mid": v(0, 67.5) * mm, "end": v(-56.15, 48.18) * mm});
            skLineSegment(sketch, "E94.9", {"start": v(60, 40.3) * mm, "end": v(60, -40.3) * mm});
            skArc(sketch, "E94.10", {"start": v(-56.15, -48.18) * mm, "mid": v(0, -67.5) * mm, "end": v(56.15, -48.18) * mm});
            skLineSegment(sketch, "E94.11", {"start": v(-60, 40.3) * mm, "end": v(-60, -40.3) * mm});
            skArc(sketch, "E94.12", {"start": v(-56.15, 48.18) * mm, "mid": v(-58.99, 44.68) * mm, "end": v(-60, 40.3) * mm});
            skArc(sketch, "E94.13", {"start": v(-60, -40.3) * mm, "mid": v(-58.99, -44.68) * mm, "end": v(-56.15, -48.18) * mm});
            skArc(sketch, "E94.14", {"start": v(56.15, -48.18) * mm, "mid": v(58.99, -44.68) * mm, "end": v(60, -40.3) * mm});
            skArc(sketch, "E94.15", {"start": v(60, 40.3) * mm, "mid": v(58.99, 44.68) * mm, "end": v(56.15, 48.18) * mm});
            skSolve(sketch);
        }
        {
            var Q0;
            Q0 = qSketchRegion(id + "F16", true);
            var Q1;
            Q1=makeQuery(id+"F2.opExtrude","CAP_FACE",FACE,{"disambiguationData":[OSD([sQuery(id+"F0.wireOp",EDGE,"E12"),sQuery(id+"F0.wireOp",EDGE,"E13"),sQuery(id+"F0.wireOp",EDGE,"E14"),sQuery(id+"F0.wireOp",EDGE,"E15"),sQuery(id+"F0.wireOp",EDGE,"E17.filletArc"),sQuery(id+"F0.wireOp",EDGE,"E18.filletArc"),sQuery(id+"F0.wireOp",EDGE,"E19.filletArc"),sQuery(id+"F0.wireOp",EDGE,"E20.filletArc"),sQuery(id+"F0.wireOp",EDGE,"E25.0"),sQuery(id+"F0.wireOp",EDGE,"E25.1"),sQuery(id+"F0.wireOp",EDGE,"E25.2"),sQuery(id+"F0.wireOp",EDGE,"E25.3"),sQuery(id+"F0.wireOp",EDGE,"E25.4"),sQuery(id+"F0.wireOp",EDGE,"E25.5"),sQuery(id+"F0.wireOp",EDGE,"E25.6"),sQuery(id+"F0.wireOp",EDGE,"E25.7")])],"isStart":false});
            extrude(context, id + "F17", {"entities" : qUnion([Q0]), "endBound" : BoundingType.UP_TO_SURFACE, "endBoundEntityFace" : qUnion([Q1]), "depth" : 25 * mm});
        }
    });
